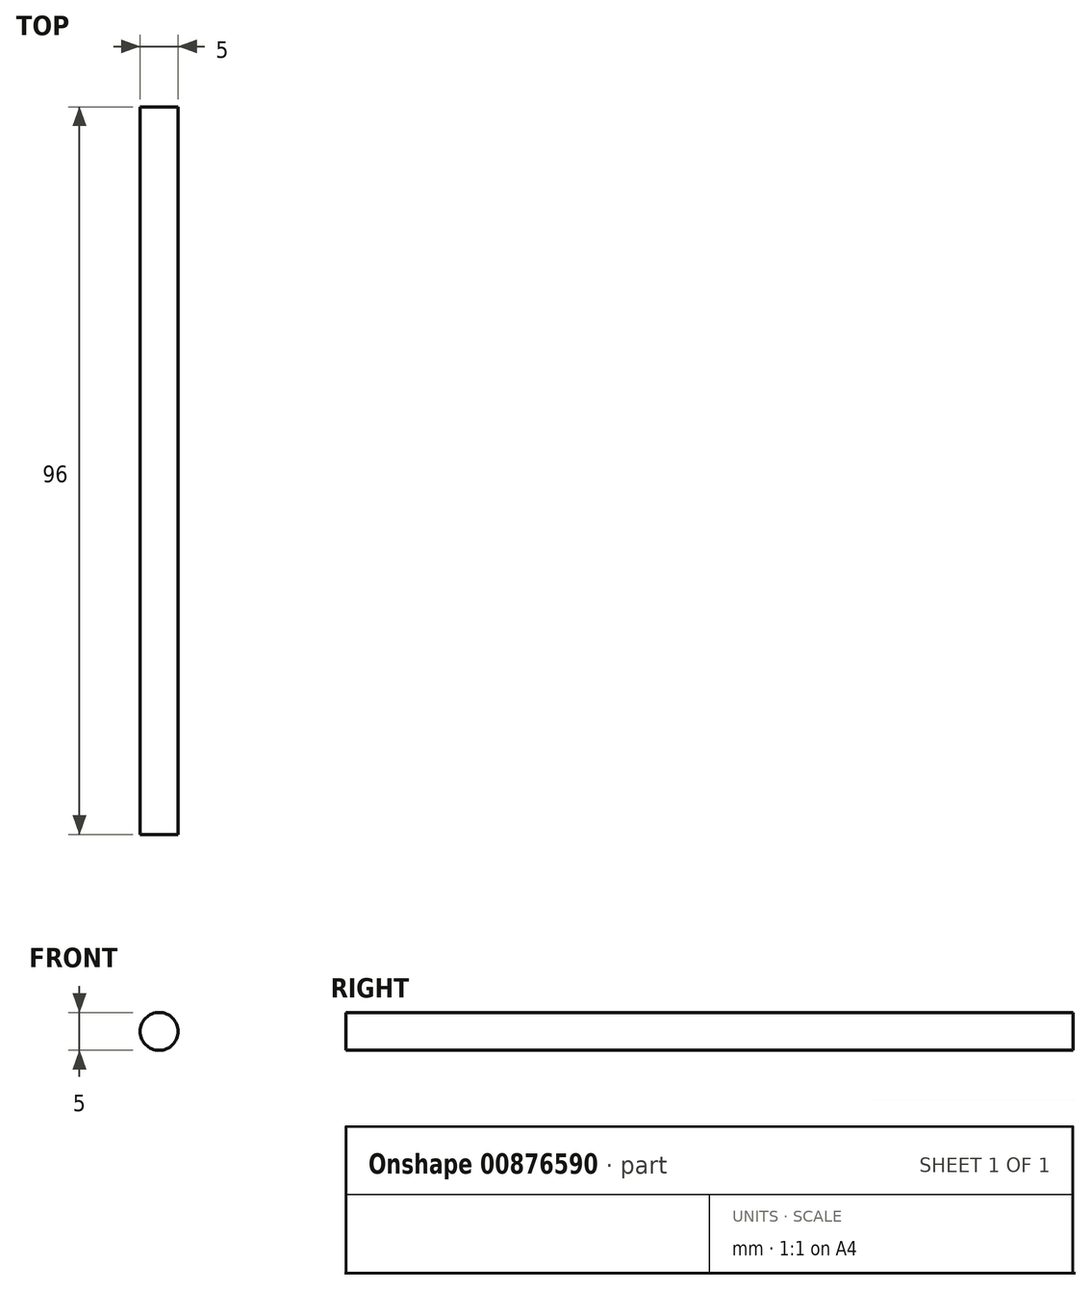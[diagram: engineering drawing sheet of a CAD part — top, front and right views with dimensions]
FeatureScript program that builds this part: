
annotation { "Feature Type Name" : "Feature", "Feature Type Description" : "" }
export const myFeature = defineFeature(function(context is Context, id is Id, definition is map)
    precondition{}
    {
        {
            var Q0;
            Q0=qCreatedBy(makeId("Front.planeOp"),FACE);
            var sketch = newSketch(context, id + "F0", { "sketchPlane" : qUnion([Q0])});
            skCircle(sketch, "E0", {"center": v(0, 0) * mm, "radius": 2.5 * mm});
            skSolve(sketch);
        }
        {
            var Q0;
            Q0=makeQuery(id+"F0.imprint","IMPRINT",FACE,{"disambiguationData":[TD([[makeQuery(id+"F0.imprint","IMPRINT",EDGE,{"derivedFrom":sQuery(id+"F0.wireOp",EDGE,"E0")}),1.0]])]});
            extrude(context, id + "F1", {"entities" : qUnion([Q0]), "depth" : 96 * mm, "offsetDistance" : 25 * mm});
        }
    });
